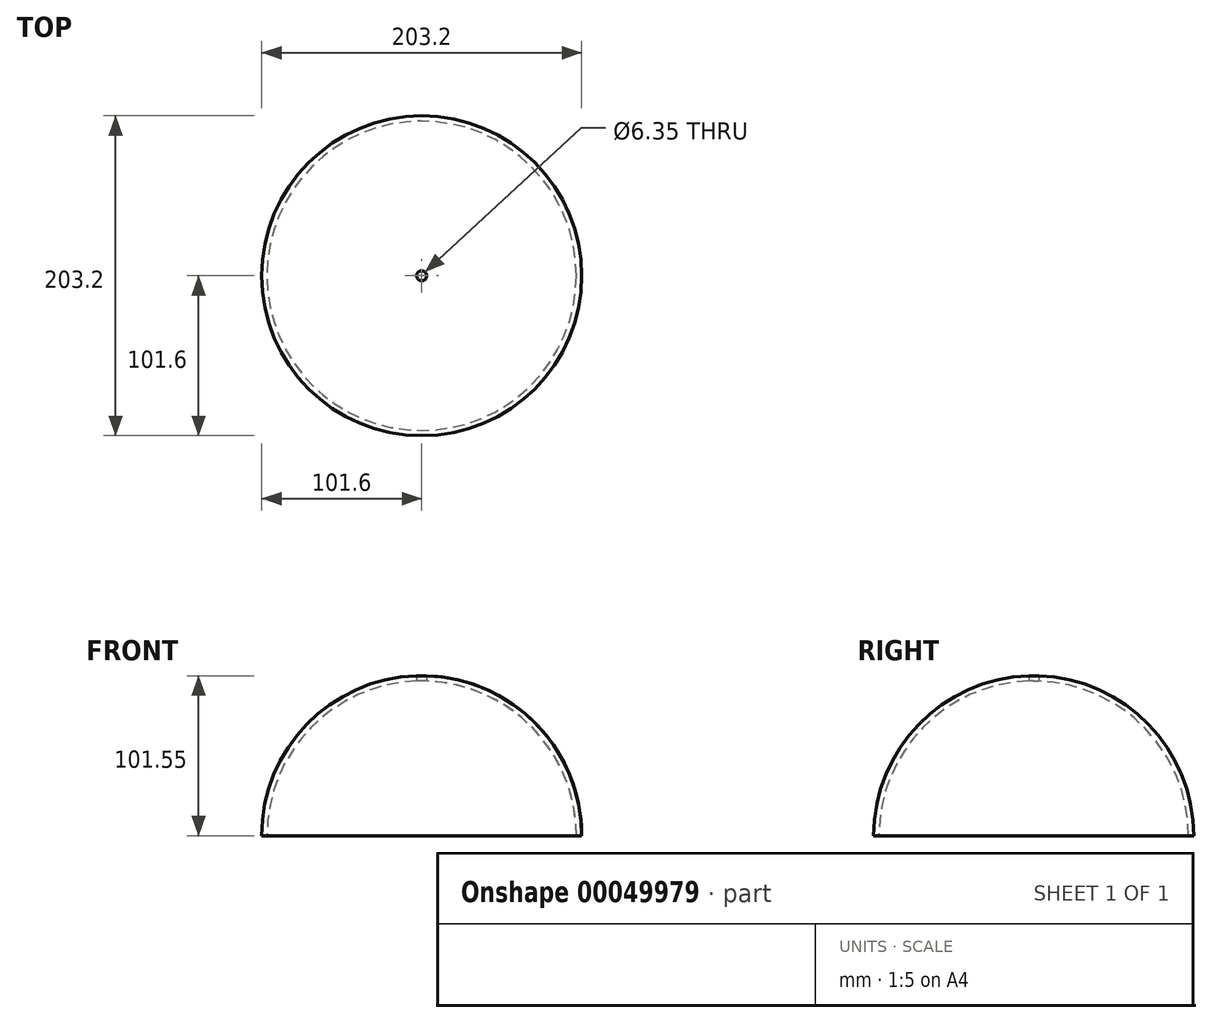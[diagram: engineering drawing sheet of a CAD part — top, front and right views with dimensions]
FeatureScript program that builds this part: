
annotation { "Feature Type Name" : "Feature", "Feature Type Description" : "" }
export const myFeature = defineFeature(function(context is Context, id is Id, definition is map)
    precondition{}
    {
        {
            var Q0;
            Q0=qCreatedBy(makeId("Front.planeOp"),FACE);
            var sketch = newSketch(context, id + "F0", { "sketchPlane" : qUnion([Q0])});
            skArc(sketch, "E0", {"start": v(98.25, 0) * mm, "mid": v(69.47, 69.47) * mm, "end": v(0, 98.25) * mm});
            skArc(sketch, "E1", {"start": v(101.6, 0) * mm, "mid": v(71.84, 71.84) * mm, "end": v(0, 101.6) * mm});
            skLineSegment(sketch, "E2", {"start": v(0, 0) * mm, "end": v(101.6, 0) * mm});
            skLineSegment(sketch, "E3", {"start": v(0, 101.6) * mm, "end": v(0, 0) * mm});
            skPoint(sketch, "E4.orphan", {"position": v(0, 25.99) * mm});
            skSolve(sketch);
        }
        {
            var Q0;
            {var subQ2=sQuery(id+"F0.wireOp",EDGE,"E0");Q0=makeQuery(id+"F0.imprint","IMPRINT",FACE,{"disambiguationData":[TD([[makeQuery(id+"F0.imprint","IMPRINT",EDGE,{"derivedFrom":subQ2}),-1.0]])]});}
            var Q1;
            Q1=sQuery(id+"F0.wireOp",EDGE,"E3");
            revolve(context, id + "F1", {"entities" : qUnion([Q0]), "axis" : qUnion([Q1]), "revolveType" : RevolveType.FULL});
        }
        {
            var Q0;
            Q0=qCreatedBy(makeId("Top.planeOp"),FACE);
            var sketch = newSketch(context, id + "F2", { "sketchPlane" : qUnion([Q0])});
            skCircle(sketch, "E5", {"center": v(0, 0) * mm, "radius": 3.18 * mm});
            skSolve(sketch);
        }
        {
            var Q0;
            Q0=makeQuery(id+"F2.imprint","IMPRINT",FACE,{"disambiguationData":[TD([[makeQuery(id+"F2.imprint","IMPRINT",EDGE,{"derivedFrom":sQuery(id+"F2.wireOp",EDGE,"E5")}),1.0]])]});
            extrude(context, id + "F3", {"entities" : qUnion([Q0]), "operationType" : NewBodyOperationType.REMOVE, "endBound" : BoundingType.THROUGH_ALL, "depth" : 25.4 * mm});
        }
    });
